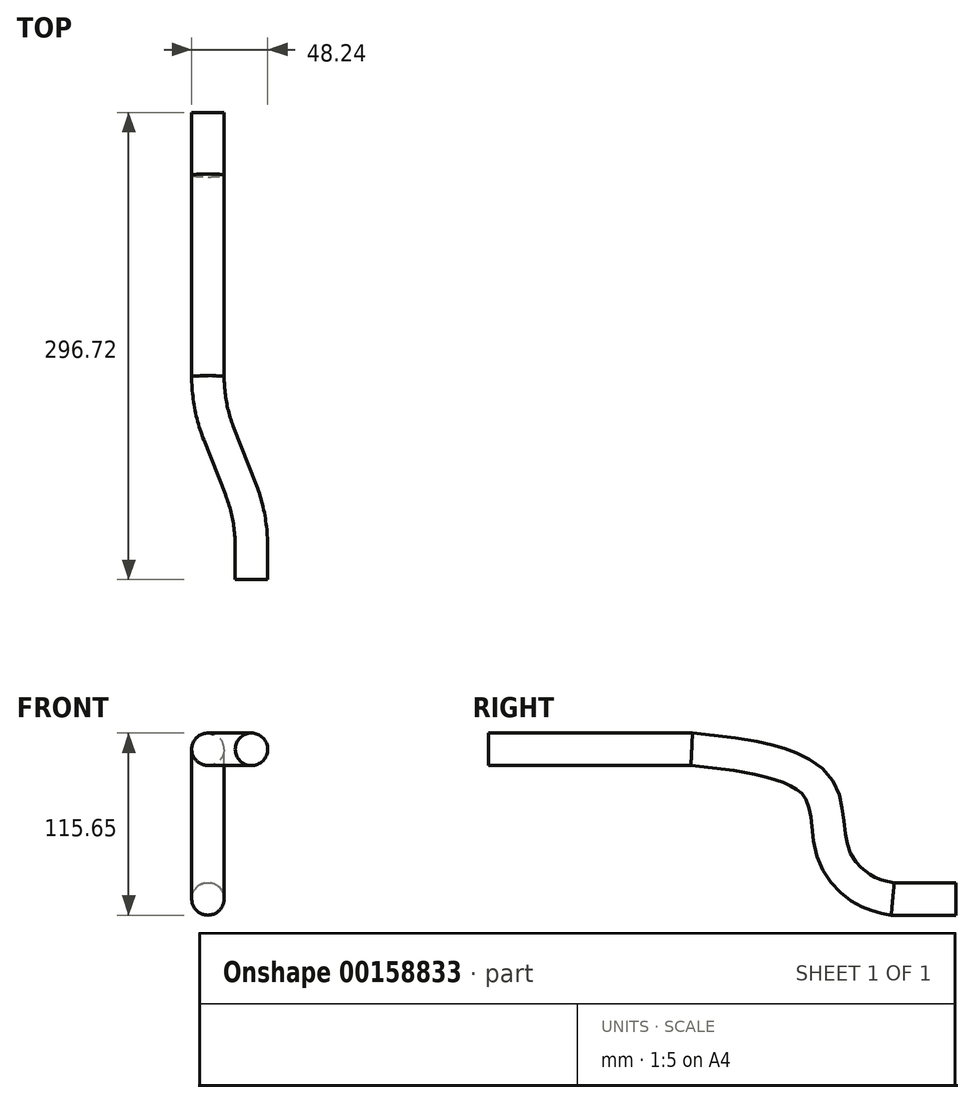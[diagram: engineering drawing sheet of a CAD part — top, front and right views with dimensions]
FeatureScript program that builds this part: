
annotation { "Feature Type Name" : "Feature", "Feature Type Description" : "" }
export const myFeature = defineFeature(function(context is Context, id is Id, definition is map)
    precondition{}
    {
        {
            var Q0;
            Q0=qCreatedBy(makeId("Top.planeOp"),FACE);
            var sketch = newSketch(context, id + "F0", { "sketchPlane" : qUnion([Q0])});
            skLineSegment(sketch, "E0", {"start": v(0, 0) * mm, "end": v(0, 150) * mm, "construction": true});
            skLineSegment(sketch, "E1", {"start": v(0, 150) * mm, "end": v(-27.64, 150) * mm, "construction": true});
            skLineSegment(sketch, "E2", {"start": v(-27.64, 150) * mm, "end": v(-27.64, 129.03) * mm});
            skLineSegment(sketch, "E3", {"start": v(-20.65, 92.3) * mm, "end": v(-6.99, 57.7) * mm});
            skLineSegment(sketch, "E4", {"start": v(0, 0) * mm, "end": v(0, 20.97) * mm});
            skPoint(sketch, "E5.visualSharp", {"position": v(-27.64, 110) * mm});
            skArc(sketch, "E5.filletArc", {"start": v(-27.64, 129.03) * mm, "mid": v(-25.88, 110.34) * mm, "end": v(-20.65, 92.3) * mm});
            skPoint(sketch, "E6.visualSharp", {"position": v(0, 40) * mm});
            skLineSegment(sketch, "E7", {"start": v(0, 20.97) * mm, "end": v(0, 20.97) * mm});
            skLineSegment(sketch, "E8", {"start": v(-6.99, 57.7) * mm, "end": v(-6.99, 57.7) * mm});
            skArc(sketch, "E9.filletArc", {"start": v(0, 20.97) * mm, "mid": v(-1.76, 39.66) * mm, "end": v(-6.99, 57.7) * mm});
            skSolve(sketch);
        }
        {
            var Q0;
            Q0=qCreatedBy(makeId("Right.planeOp"),FACE);
            cPlane(context, id + "F1", {"entities" : qUnion([Q0]), "cplaneType" : CPlaneType.OFFSET, "offset" : 27.64 * mm, "oppositeDirection" : true, "width" : 150 * mm, "height" : 150 * mm});
        }
        {
            var Q0;
            Q0=qCreatedBy(id+"F1.planeOp",FACE);
            var sketch = newSketch(context, id + "F2", { "sketchPlane" : qUnion([Q0])});
            skPoint(sketch, "E10.0", {"position": v(150, 0) * mm});
            skLineSegment(sketch, "E11", {"start": v(150, -95.05) * mm, "end": v(296.72, -95.05) * mm, "construction": true});
            skLineSegment(sketch, "E12", {"start": v(296.72, -95.05) * mm, "end": v(267.41, -95.05) * mm});
            skPoint(sketch, "E13.visualSharp", {"position": v(256.72, -95.05) * mm});
            skLineSegment(sketch, "E14", {"start": v(150, 0) * mm, "end": v(150, -95.05) * mm, "construction": true});
            skPoint(sketch, "E15.0", {"position": v(129.03, 0) * mm});
            skFitSpline(sketch, "E16", {"points": [v(256.72, -95.05) * mm, v(239.6, -89.8) * mm, v(218.87, -66.15) * mm, v(209.8, -25.33) * mm, v(169.95, -5.57) * mm, v(129.03, 0) * mm], "startDerivative": vector(-115.42, 21) * mm, "endDerivative": vector(-179.25, 17.08) * mm});
            skLineSegment(sketch, "E17", {"start": v(256.72, -95.05) * mm, "end": v(296.72, -95.05) * mm});
            skSolve(sketch);
        }
        {
            var Q0;
            Q0=qCreatedBy(makeId("Front.planeOp"),FACE);
            var sketch = newSketch(context, id + "F3", { "sketchPlane" : qUnion([Q0])});
            skCircle(sketch, "E18", {"center": v(0, 0) * mm, "radius": 10.3 * mm});
            skSolve(sketch);
        }
        {
            var Q0;
            Q0 = qSketchRegion(id + "F3", true);
            var Q1;
            Q1=sQuery(id+"F0.wireOp",EDGE,"E4");
            var Q2;
            Q2=sQuery(id+"F0.wireOp",EDGE,"E9.filletArc");
            var Q3;
            Q3=sQuery(id+"F0.wireOp",EDGE,"E3");
            var Q4;
            Q4=sQuery(id+"F0.wireOp",EDGE,"E5.filletArc");
            var Q5;
            Q5=sQuery(id+"F2.wireOp",EDGE,"E16");
            var Q6;
            Q6=sQuery(id+"F2.wireOp",EDGE,"E17");
            sweep(context, id + "F4", {"profiles" : qUnion([Q0]), "path" : qUnion([Q1, Q2, Q3, Q4, Q5, Q6])});
        }
    });
